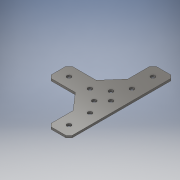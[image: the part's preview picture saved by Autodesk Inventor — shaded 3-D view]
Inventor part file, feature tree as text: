
AUTODESK INVENTOR PART (.ipt)
format: ipt  version: 2017 (Build 210142000, 142)  size: 122,368 bytes
history: native  units: in
note: dims shown in document units (in); Inventor stores cm internally (conversion verified against a paired STEP export)
features: extrude x1, sketch x1
ambient origin geometry x8: Origin, YZ Plane, XZ Plane, XY Plane, X Axis, Y Axis, Z Axis, Center Point
bodies: Solid1 (feature_tree)
feature tree (2):
  extrude  "Extrusion1"  [1 undecoded]
  sketch  "Sketch1"  dims[d38=0.1in d39=0.0in]
note: 1 required parameter value undecoded (feature->parameter linkage not recoverable at this tier; creation-order binding heuristic only, values carry confidence <= 0.55)
